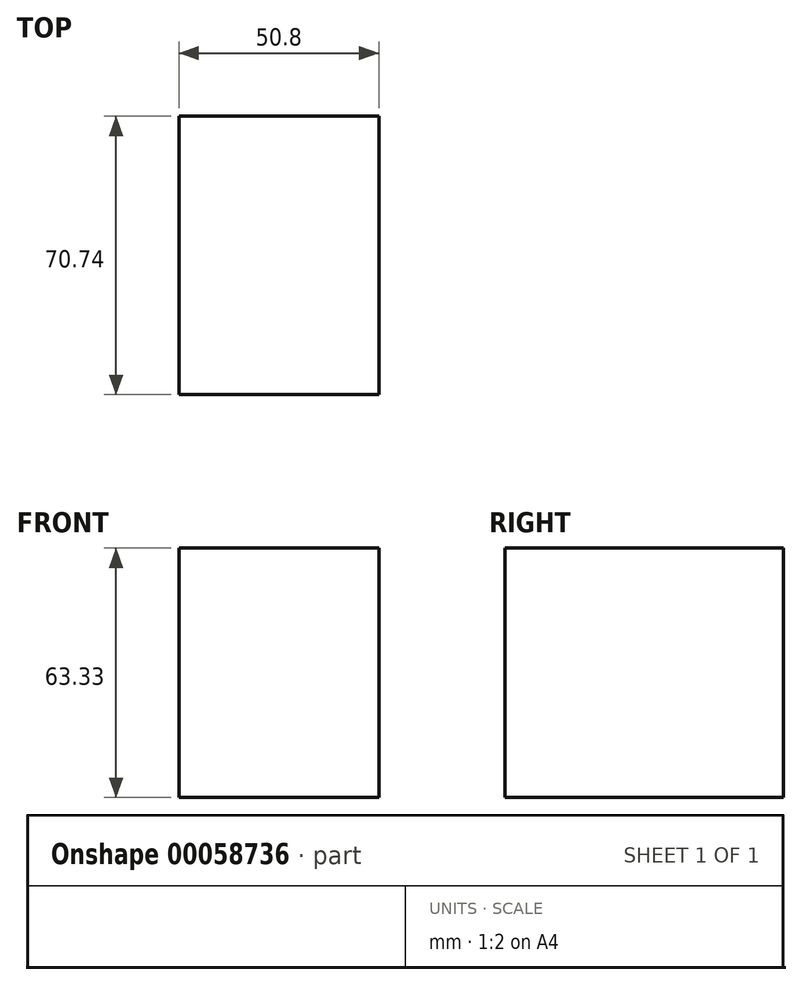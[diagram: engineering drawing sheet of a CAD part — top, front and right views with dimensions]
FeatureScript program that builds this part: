
annotation { "Feature Type Name" : "Feature", "Feature Type Description" : "" }
export const myFeature = defineFeature(function(context is Context, id is Id, definition is map)
    precondition{}
    {
        {
            var Q0;
            Q0=qCreatedBy(makeId("Right.planeOp"),FACE);
            var sketch = newSketch(context, id + "F0", { "sketchPlane" : qUnion([Q0])});
            skLineSegment(sketch, "E0.bottom", {"start": v(-35.94, 29.8) * mm, "end": v(34.8, 29.8) * mm});
            skLineSegment(sketch, "E0.top", {"start": v(-35.94, -33.52) * mm, "end": v(34.8, -33.52) * mm});
            skLineSegment(sketch, "E0.left", {"start": v(-35.94, 29.8) * mm, "end": v(-35.94, -33.52) * mm});
            skLineSegment(sketch, "E0.right", {"start": v(34.8, 29.8) * mm, "end": v(34.8, -33.52) * mm});
            skSolve(sketch);
        }
        {
            var Q0;
            Q0 = qSketchRegion(id + "F0", true);
            extrude(context, id + "F1", {"entities" : qUnion([Q0]), "depth" : 25.4 * mm, "hasSecondDirection" : true, "secondDirectionOppositeDirection" : true, "secondDirectionDepth" : 25.4 * mm});
        }
    });
